# Revit family: KOBE_4000K_4700LM
name_source: partatom
category: Lighting Fixtures
units: mm (PartAtom-declared; Revit-internal decimal feet)

## family parameters
Always vertical = Yes
Cut with Voids When Loaded = No
Host = Ceiling
Light Source = Yes
OmniClass Number = 23.80.70.11
OmniClass Title = Luminaries for Internal Lighting
Part Type = Normal
Room Calculation Point = No
Round Connector Dimension = Use Diameter
Shared = No

## types (1)
- Type 1
    Alimentation Driver = 220-240V AC
    Alimentation luminaire = 20-42V dc / 900mA
    Angle d'éclairage = 60°
    Color Filter = 16777215
    Default Elevation = 0 mm  [stored 0 ft]
    Dimensions = 595x595x18 mm
    Dimensions d’encastrement = 595x595x18 mm
    Dimming Lamp Color Temperature Shift = <None>
    Driver = Driver Tuv - No flicker
    Durée de vie = 50 000 heures
    Emit Shape Visible in Rendering = No
    Emit from Rectangle Length = 1219 mm
    Emit from Rectangle Width = 610 mm
    Fintion = Blanc
    Flux lumineux = 4700 lm
    IRC = >80
    Maintien du flux = L80B10 (50 000 heures)
    Matériau = Acier
    Photometric Web File = google_eulumdat_converter (7).ies
    Puissance nominale = 36W
    SDCM = <3
    Température = 4000K
    Tilt Angle = 90.00°
    Type = Plafonnier
    Type de lampe = LED Seoul

note: [stored X ft] marks values corroborated as IEEE doubles in the binary element streams (Revit-internal decimal feet)

## geometry (parser evidence)
native form markers: Sweep x3
no freeform markers — native parametric forms only
